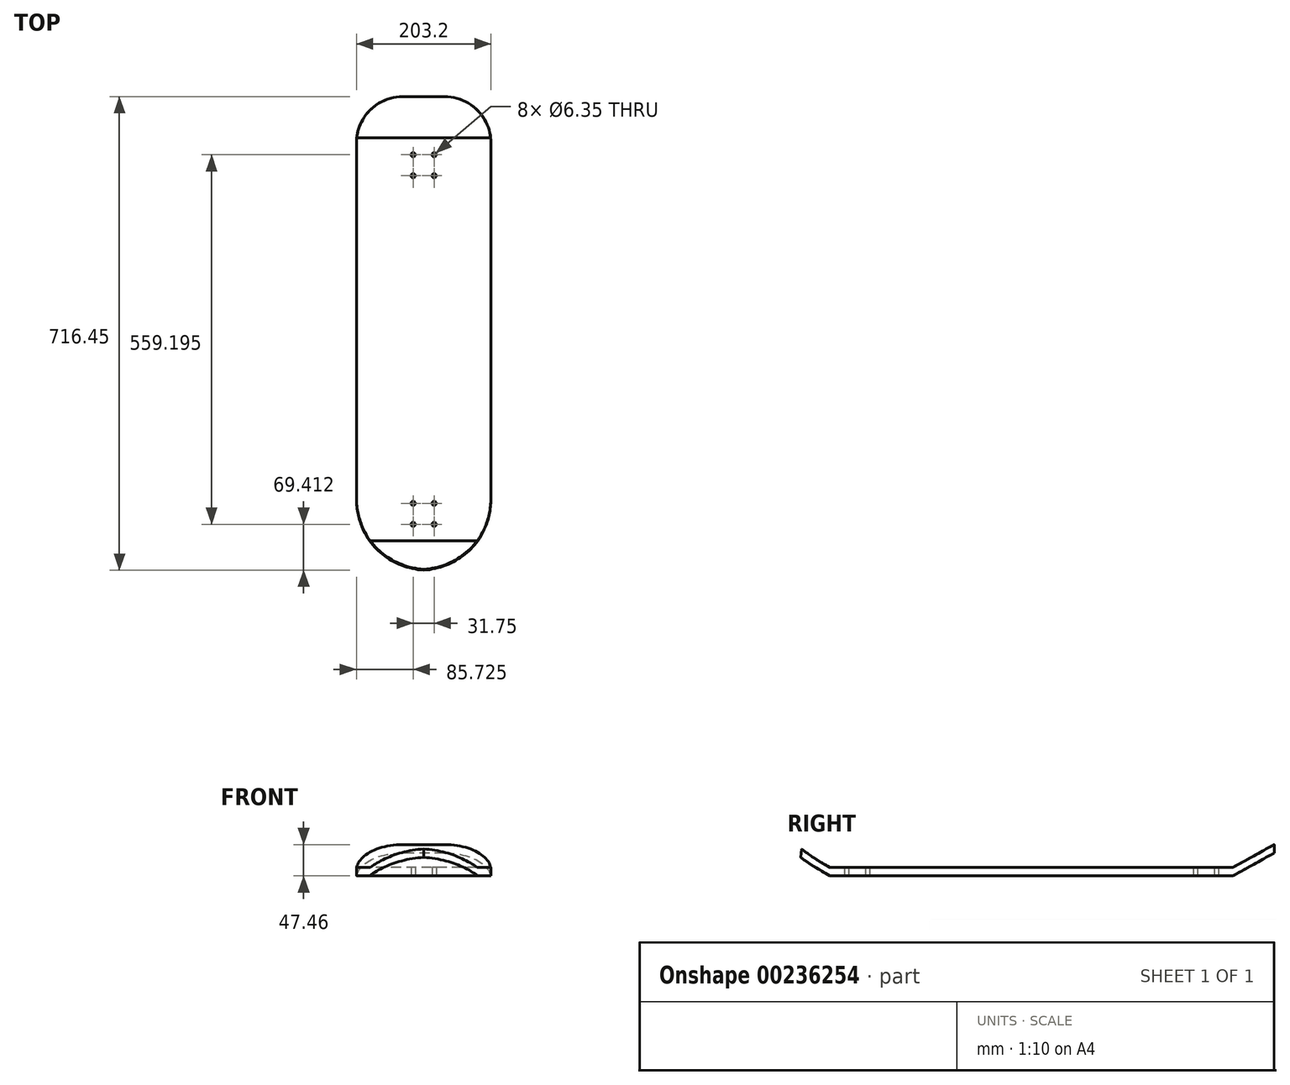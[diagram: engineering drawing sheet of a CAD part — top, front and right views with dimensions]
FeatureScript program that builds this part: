
annotation { "Feature Type Name" : "Feature", "Feature Type Description" : "" }
export const myFeature = defineFeature(function(context is Context, id is Id, definition is map)
    precondition{}
    {
        {
            var Q0;
            Q0=qCreatedBy(makeId("Top.planeOp"),FACE);
            var sketch = newSketch(context, id + "F0", { "sketchPlane" : qUnion([Q0])});
            skLineSegment(sketch, "E0.bottom", {"start": v(101.6, -304.8) * mm, "end": v(-101.6, -304.8) * mm});
            skLineSegment(sketch, "E0.top", {"start": v(101.6, 304.8) * mm, "end": v(-101.6, 304.8) * mm});
            skLineSegment(sketch, "E0.left", {"start": v(101.6, -304.8) * mm, "end": v(101.6, 304.8) * mm});
            skLineSegment(sketch, "E0.right", {"start": v(-101.6, -304.8) * mm, "end": v(-101.6, 304.8) * mm});
            skPoint(sketch, "E0.middle", {"position": v(0, 0) * mm});
            skPoint(sketch, "E1.middle", {"position": v(0, 263.72) * mm});
            skCircle(sketch, "E2", {"center": v(-15.87, 279.6) * mm, "radius": 3.18 * mm});
            skCircle(sketch, "E3", {"center": v(15.88, 279.6) * mm, "radius": 3.18 * mm});
            skCircle(sketch, "E4", {"center": v(-15.87, 247.85) * mm, "radius": 3.18 * mm});
            skCircle(sketch, "E5", {"center": v(15.88, 247.85) * mm, "radius": 3.18 * mm});
            skPoint(sketch, "E1.right.end.orphan", {"position": v(-25.4, 289.12) * mm});
            skPoint(sketch, "E1.bottom.end.orphan", {"position": v(-25.4, 238.32) * mm});
            skPoint(sketch, "E1.left.end.orphan", {"position": v(25.4, 289.12) * mm});
            skPoint(sketch, "E1.left.start.orphan", {"position": v(25.4, 238.32) * mm});
            skCircle(sketch, "E6.MirrorC", {"center": v(-15.87, -247.85) * mm, "radius": 3.18 * mm});
            skCircle(sketch, "E7.MirrorC", {"center": v(15.88, -247.85) * mm, "radius": 3.18 * mm});
            skCircle(sketch, "E8.MirrorC", {"center": v(15.88, -279.6) * mm, "radius": 3.18 * mm});
            skCircle(sketch, "E9.MirrorC", {"center": v(-15.87, -279.6) * mm, "radius": 3.18 * mm});
            skSolve(sketch);
        }
        {
            var Q0;
            Q0 = qSketchRegion(id + "F0", true);
            extrude(context, id + "F1", {"entities" : qUnion([Q0]), "endBound" : BoundingType.SYMMETRIC, "depth" : 12.7 * mm});
        }
        {
            var Q0;
            Q0=qCreatedBy(makeId("Right.planeOp"),FACE);
            var sketch = newSketch(context, id + "F2", { "sketchPlane" : qUnion([Q0])});
            skFitSpline(sketch, "E10", {"points": [v(304.46, 0) * mm, v(335.02, 16.78) * mm, v(367.39, 34.76) * mm], "startDerivative": vector(61.64, 33.74) * mm, "endDerivative": vector(64.2, 35.77) * mm});
            skFitSpline(sketch, "E11", {"points": [v(-305.35, 0) * mm, v(-330.92, 15.38) * mm, v(-349.25, 28.16) * mm], "startDerivative": vector(-49.88, 29) * mm, "endDerivative": vector(-37.63, 27.28) * mm});
            skSolve(sketch);
        }
        {
            var Q0;
            Q0=makeQuery(id+"F1.opExtrude","SWEPT_FACE",FACE,{"disambiguationData":[OSD([sQuery(id+"F0.wireOp",EDGE,"E0.top")])]});
            var Q1;
            Q1=sQuery(id+"F2.wireOp",EDGE,"E10");
            sweep(context, id + "F3", {"operationType" : NewBodyOperationType.ADD, "profiles" : qUnion([Q0]), "path" : qUnion([Q1])});
        }
        {
            var Q0;
            Q0=makeQuery(id+"F1.opExtrude","SWEPT_FACE",FACE,{"disambiguationData":[OSD([sQuery(id+"F0.wireOp",EDGE,"E0.bottom")])]});
            var Q1;
            Q1=sQuery(id+"F2.wireOp",EDGE,"E11");
            sweep(context, id + "F4", {"operationType" : NewBodyOperationType.ADD, "profiles" : qUnion([Q0]), "path" : qUnion([Q1])});
        }
        {
            var Q0;
            Q0=makeQuery(id+"F4.opSweep","CAP_EDGE",EDGE,{"disambiguationData":[OSD([sQuery(id+"F0.wireOp",EDGE,"E0.bottom"),sQuery(id+"F0.wireOp",EDGE,"E0.left"),sQuery(id+"F2.wireOp",VERTEX,"E11.end")])],"isStart":false});
            var Q1;
            Q1=makeQuery(id+"F4.opSweep","CAP_EDGE",EDGE,{"disambiguationData":[OSD([sQuery(id+"F0.wireOp",EDGE,"E0.bottom"),sQuery(id+"F0.wireOp",EDGE,"E0.right"),sQuery(id+"F2.wireOp",VERTEX,"E11.end")])],"isStart":false});
            fillet(context, id + "F5", {"entities" : qUnion([Q0, Q1]), "radius" : 110.38 * mm, "tangentPropagation" : true, "allowEdgeOverflow" : false});
        }
        {
            var Q0;
            Q0=makeQuery(id+"F3.opSweep","CAP_EDGE",EDGE,{"disambiguationData":[OSD([sQuery(id+"F0.wireOp",EDGE,"E0.top"),sQuery(id+"F0.wireOp",EDGE,"E0.left"),sQuery(id+"F2.wireOp",VERTEX,"E10.end")])],"isStart":false});
            var Q1;
            Q1=makeQuery(id+"F3.opSweep","CAP_EDGE",EDGE,{"disambiguationData":[OSD([sQuery(id+"F0.wireOp",EDGE,"E0.top"),sQuery(id+"F0.wireOp",EDGE,"E0.right"),sQuery(id+"F2.wireOp",VERTEX,"E10.end")])],"isStart":false});
            fillet(context, id + "F6", {"entities" : qUnion([Q0, Q1]), "radius" : 69.9 * mm, "tangentPropagation" : true, "allowEdgeOverflow" : false});
        }
    });
